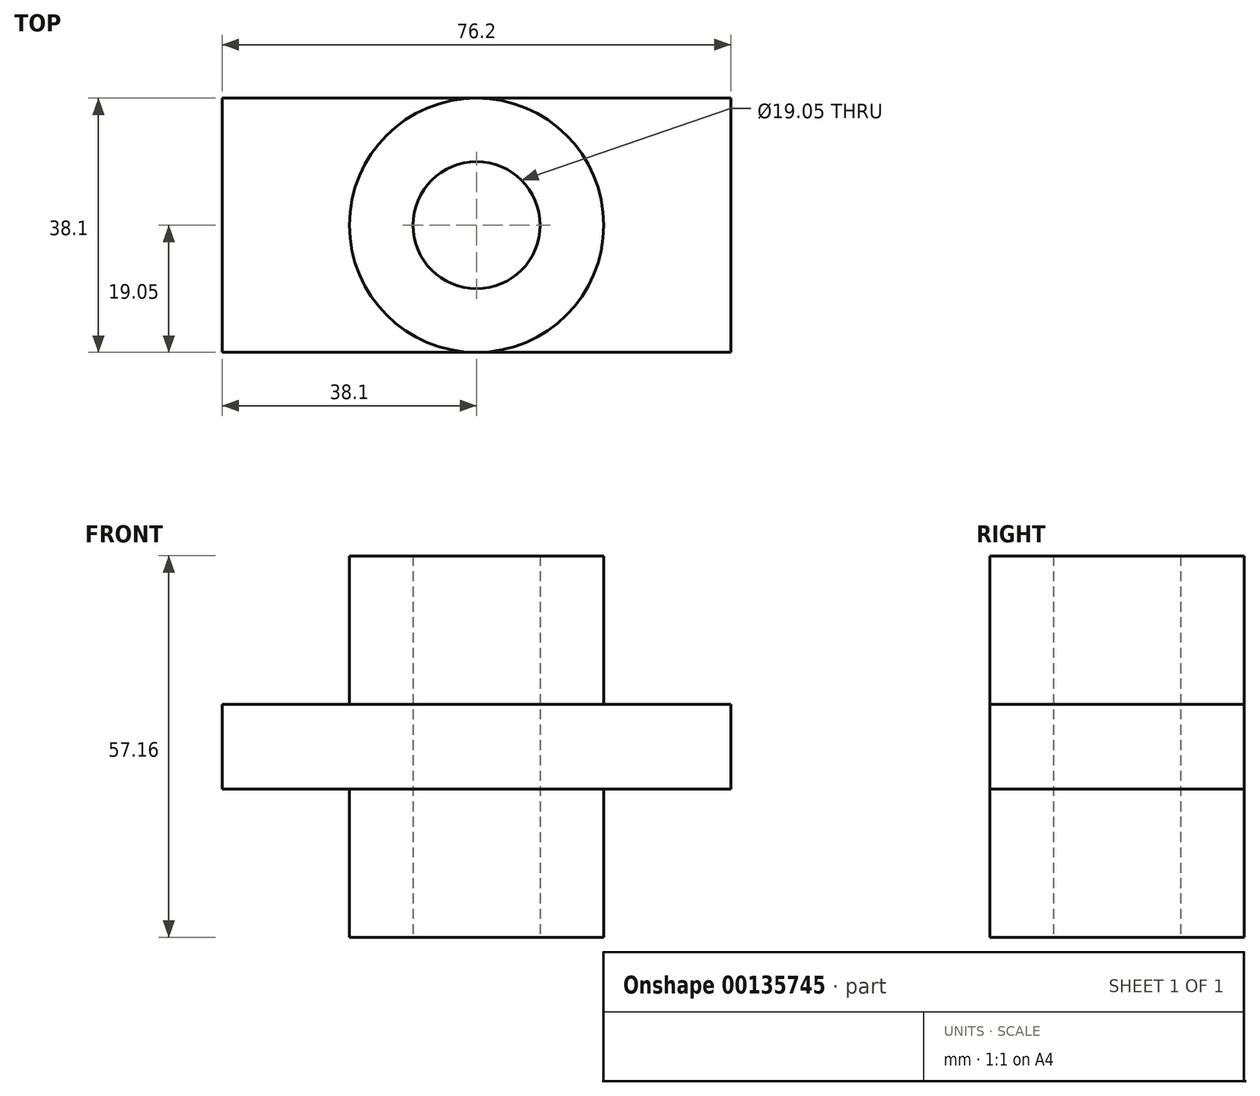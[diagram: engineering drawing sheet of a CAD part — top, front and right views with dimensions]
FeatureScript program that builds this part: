
annotation { "Feature Type Name" : "Feature", "Feature Type Description" : "" }
export const myFeature = defineFeature(function(context is Context, id is Id, definition is map)
    precondition{}
    {
        {
            var Q0;
            Q0=qCreatedBy(makeId("Top.planeOp"),FACE);
            var sketch = newSketch(context, id + "F0", { "sketchPlane" : qUnion([Q0])});
            skLineSegment(sketch, "E0", {"start": v(0, -19.05) * mm, "end": v(0, 19.05) * mm});
            skCircle(sketch, "E1", {"center": v(0, 0) * mm, "radius": 12.7 * mm, "construction": true});
            skCircle(sketch, "E2", {"center": v(0, 0) * mm, "radius": 9.52 * mm});
            skCircle(sketch, "E3", {"center": v(0, 0) * mm, "radius": 19.05 * mm});
            skLineSegment(sketch, "E4", {"start": v(0, 0) * mm, "end": v(9.52, 0) * mm, "construction": true});
            skLineSegment(sketch, "E5", {"start": v(0, 0) * mm, "end": v(0, -19.05) * mm, "construction": true});
            skSolve(sketch);
        }
        {
            var Q0;
            Q0 = qSketchRegion(id + "F0", true);
            extrude(context, id + "F1", {"entities" : qUnion([Q0]), "endBound" : BoundingType.SYMMETRIC, "depth" : 57.15 * mm});
        }
        {
            var Q0;
            Q0=qCreatedBy(makeId("Front.planeOp"),FACE);
            var sketch = newSketch(context, id + "F2", { "sketchPlane" : qUnion([Q0])});
            skLineSegment(sketch, "E6.bottom", {"start": v(-38.1, -6.35) * mm, "end": v(38.1, -6.35) * mm});
            skLineSegment(sketch, "E6.top", {"start": v(-38.1, 6.35) * mm, "end": v(38.1, 6.35) * mm});
            skLineSegment(sketch, "E6.left", {"start": v(-38.1, -6.35) * mm, "end": v(-38.1, 6.35) * mm});
            skLineSegment(sketch, "E6.right", {"start": v(38.1, -6.35) * mm, "end": v(38.1, 6.35) * mm});
            skLineSegment(sketch, "E7", {"start": v(0, 0) * mm, "end": v(0, -6.35) * mm, "construction": true});
            skLineSegment(sketch, "E8", {"start": v(38.1, 0) * mm, "end": v(0, 0) * mm, "construction": true});
            skPoint(sketch, "E8.startSnap0", {"position": v(38.1, 0) * mm});
            skSolve(sketch);
        }
        {
            var Q0;
            Q0 = qSketchRegion(id + "F2", true);
            extrude(context, id + "F3", {"entities" : qUnion([Q0]), "operationType" : NewBodyOperationType.ADD, "oppositeDirection" : true, "depth" : 19.05 * mm, "hasSecondDirection" : true, "secondDirectionOppositeDirection" : false, "secondDirectionDepth" : 19.05 * mm});
        }
        {
            var Q0;
            Q0=makeQuery(id+"F3.boolean.opBoolean","SPLIT",FACE,{"disambiguationData":[TD([makeQuery(id+"F1.opExtrude","SWEPT_FACE",FACE,{"disambiguationData":[OSD([sQuery(id+"F0.wireOp",EDGE,"E2")])]})])],"derivedFrom":makeQuery(id+"F3.opExtrude","SWEPT_FACE",FACE,{"disambiguationData":[OSD([sQuery(id+"F2.wireOp",EDGE,"E6.top")])]})});
            var sketch = newSketch(context, id + "F4", { "sketchPlane" : qUnion([Q0])});
            skCircle(sketch, "E9.0.0", {"center": v(0, 0) * mm, "radius": 9.52 * mm});
            skSolve(sketch);
        }
        {
            var Q0;
            Q0 = qSketchRegion(id + "F4", true);
            extrude(context, id + "F5", {"entities" : qUnion([Q0]), "operationType" : NewBodyOperationType.REMOVE, "endBound" : BoundingType.THROUGH_ALL, "oppositeDirection" : true, "depth" : 25.4 * mm});
        }
    });
